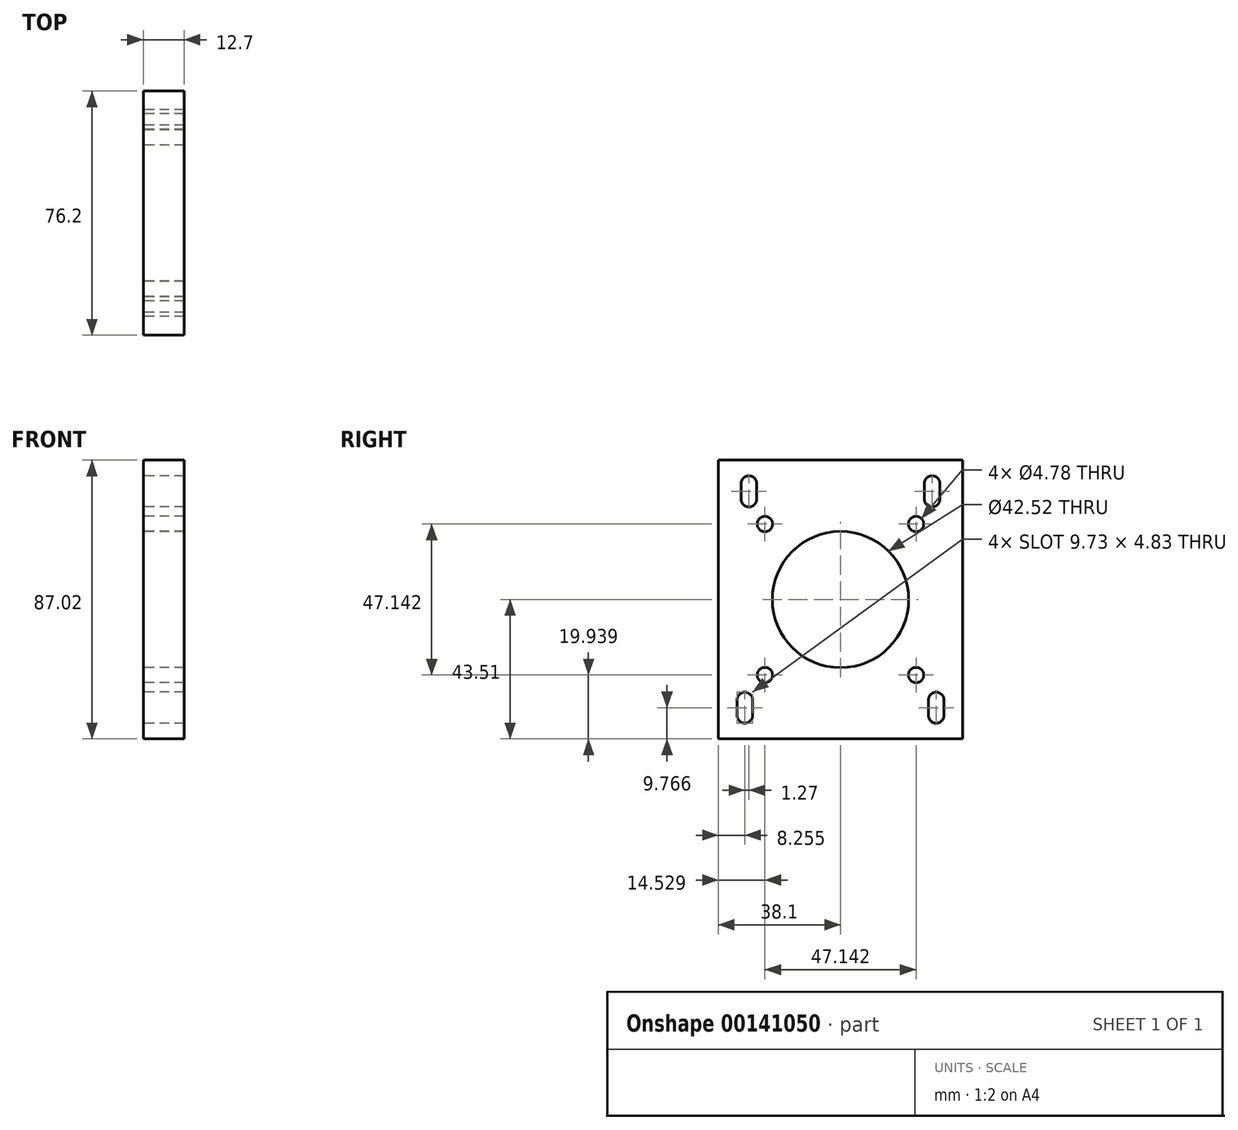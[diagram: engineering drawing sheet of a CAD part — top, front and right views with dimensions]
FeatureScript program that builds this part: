
annotation { "Feature Type Name" : "Feature", "Feature Type Description" : "" }
export const myFeature = defineFeature(function(context is Context, id is Id, definition is map)
    precondition{}
    {
        {
            var Q0;
            Q0=qCreatedBy(makeId("Right.planeOp"),FACE);
            var sketch = newSketch(context, id + "F0", { "sketchPlane" : qUnion([Q0])});
            skLineSegment(sketch, "E0.bottom", {"start": v(-38.1, 43.51) * mm, "end": v(38.1, 43.51) * mm});
            skLineSegment(sketch, "E0.top", {"start": v(-38.1, -43.51) * mm, "end": v(38.1, -43.51) * mm});
            skLineSegment(sketch, "E0.left", {"start": v(-38.1, 43.51) * mm, "end": v(-38.1, -43.51) * mm});
            skLineSegment(sketch, "E0.right", {"start": v(38.1, 43.51) * mm, "end": v(38.1, -43.51) * mm});
            skPoint(sketch, "E0.middle", {"position": v(0, 0) * mm});
            skCircle(sketch, "E1", {"center": v(0, 0) * mm, "radius": 21.26 * mm});
            skCircle(sketch, "E2", {"center": v(-23.57, 23.57) * mm, "radius": 2.39 * mm});
            skCircle(sketch, "E3.MirrorC", {"center": v(23.57, 23.57) * mm, "radius": 2.39 * mm});
            skCircle(sketch, "E4.MirrorC", {"center": v(-23.57, -23.57) * mm, "radius": 2.39 * mm});
            skCircle(sketch, "E5.MirrorC", {"center": v(23.57, -23.57) * mm, "radius": 2.39 * mm});
            skArc(sketch, "E6", {"start": v(-27.43, -31.3) * mm, "mid": v(-29.85, -28.88) * mm, "end": v(-32.26, -31.3) * mm});
            skArc(sketch, "E7", {"start": v(-32.26, -36.2) * mm, "mid": v(-29.85, -38.6) * mm, "end": v(-27.43, -36.2) * mm});
            skLineSegment(sketch, "E8", {"start": v(-27.43, -36.2) * mm, "end": v(-27.43, -31.3) * mm});
            skLineSegment(sketch, "E9", {"start": v(-32.26, -36.2) * mm, "end": v(-32.26, -31.3) * mm});
            skLineSegment(sketch, "E10.MirrorCS", {"start": v(27.43, -36.2) * mm, "end": v(27.43, -31.3) * mm});
            skArc(sketch, "E11.MirrorCS", {"start": v(27.43, -31.3) * mm, "mid": v(29.85, -28.88) * mm, "end": v(32.26, -31.3) * mm});
            skLineSegment(sketch, "E12.MirrorCS", {"start": v(32.26, -36.2) * mm, "end": v(32.26, -31.3) * mm});
            skArc(sketch, "E13.MirrorCS", {"start": v(32.26, -36.2) * mm, "mid": v(29.85, -38.6) * mm, "end": v(27.43, -36.2) * mm});
            skArc(sketch, "E14", {"start": v(-26.16, 36.2) * mm, "mid": v(-28.58, 38.6) * mm, "end": v(-30.99, 36.2) * mm});
            skArc(sketch, "E15", {"start": v(-30.99, 31.3) * mm, "mid": v(-28.57, 28.88) * mm, "end": v(-26.16, 31.3) * mm});
            skLineSegment(sketch, "E16", {"start": v(-26.16, 36.2) * mm, "end": v(-26.16, 31.3) * mm});
            skLineSegment(sketch, "E17", {"start": v(-30.99, 36.2) * mm, "end": v(-30.99, 31.3) * mm});
            skLineSegment(sketch, "E18.MirrorCS", {"start": v(30.99, 36.2) * mm, "end": v(30.99, 31.3) * mm});
            skArc(sketch, "E19.MirrorCS", {"start": v(26.16, 36.2) * mm, "mid": v(28.58, 38.6) * mm, "end": v(30.99, 36.2) * mm});
            skLineSegment(sketch, "E20.MirrorCS", {"start": v(26.16, 36.2) * mm, "end": v(26.16, 31.3) * mm});
            skArc(sketch, "E21.MirrorCS", {"start": v(30.99, 31.3) * mm, "mid": v(28.57, 28.88) * mm, "end": v(26.16, 31.3) * mm});
            skSolve(sketch);
        }
        {
            var Q0;
            Q0 = qSketchRegion(id + "F0", true);
            extrude(context, id + "F1", {"entities" : qUnion([Q0]), "depth" : 12.7 * mm});
        }
    });
